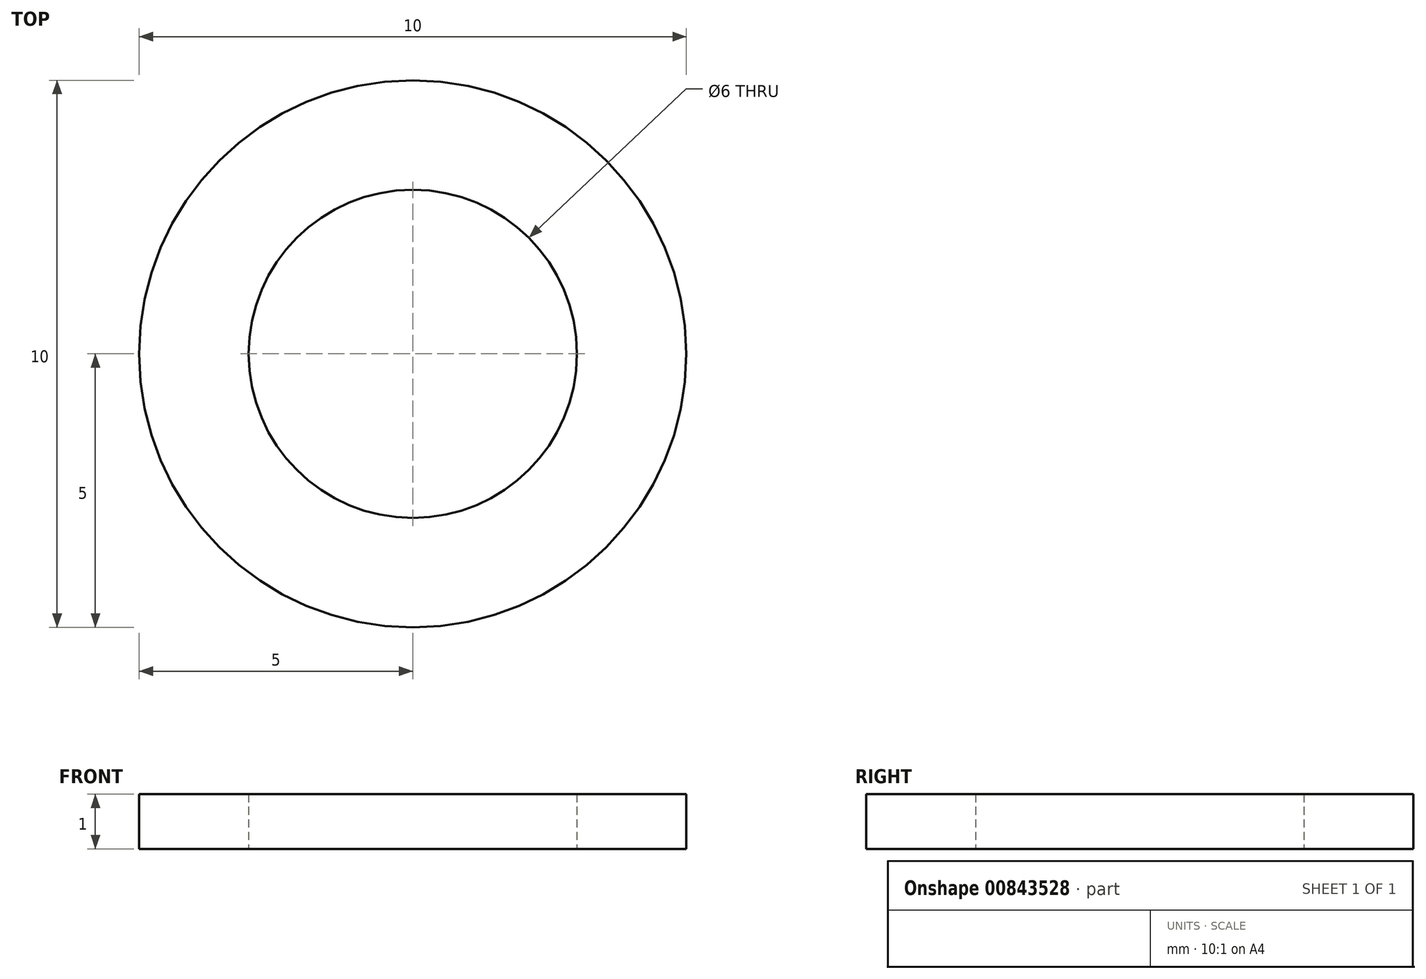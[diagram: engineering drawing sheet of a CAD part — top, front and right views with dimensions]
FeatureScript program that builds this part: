
annotation { "Feature Type Name" : "Feature", "Feature Type Description" : "" }
export const myFeature = defineFeature(function(context is Context, id is Id, definition is map)
    precondition{}
    {
        {
            var Q0;
            Q0=qCreatedBy(makeId("Top.planeOp"),FACE);
            var sketch = newSketch(context, id + "F0", { "sketchPlane" : qUnion([Q0])});
            skCircle(sketch, "E0", {"center": v(0, 0) * mm, "radius": 3 * mm});
            skCircle(sketch, "E1", {"center": v(0, 0) * mm, "radius": 5 * mm});
            skSolve(sketch);
        }
        {
            var Q0;
            Q0 = qSketchRegion(id + "F0", true);
            extrude(context, id + "F1", {"entities" : qUnion([Q0]), "depth" : 1 * mm, "offsetDistance" : 25 * mm});
        }
    });
